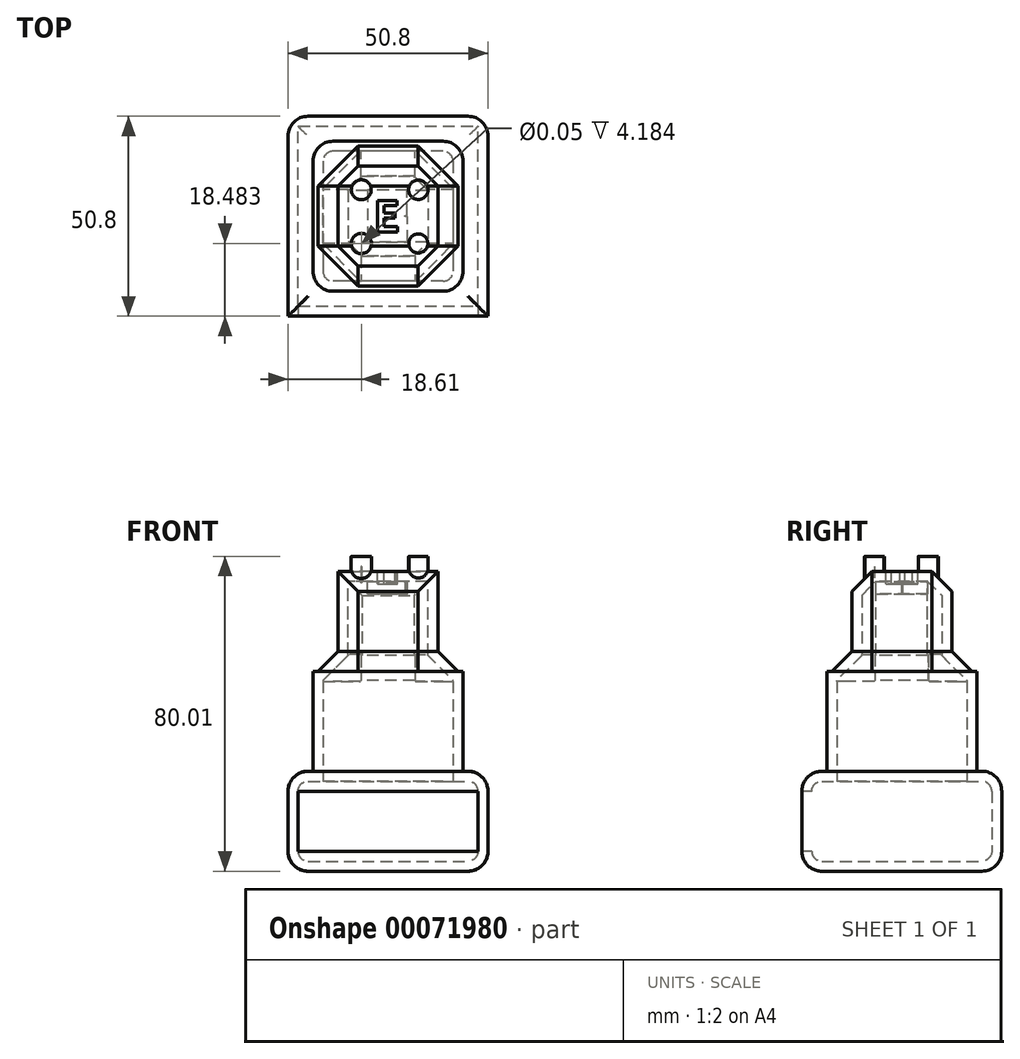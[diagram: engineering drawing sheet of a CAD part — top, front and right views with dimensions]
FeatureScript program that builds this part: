
annotation { "Feature Type Name" : "Feature", "Feature Type Description" : "" }
export const myFeature = defineFeature(function(context is Context, id is Id, definition is map)
    precondition{}
    {
        {
            var Q0;
            Q0=qCreatedBy(makeId("Top.planeOp"),FACE);
            var sketch = newSketch(context, id + "F0", { "sketchPlane" : qUnion([Q0])});
            skLineSegment(sketch, "E0.bottom", {"start": v(0, 0) * mm, "end": v(50.8, 0) * mm});
            skLineSegment(sketch, "E0.top", {"start": v(0, 50.8) * mm, "end": v(50.8, 50.8) * mm});
            skLineSegment(sketch, "E0.left", {"start": v(0, 0) * mm, "end": v(0, 50.8) * mm});
            skLineSegment(sketch, "E0.right", {"start": v(50.8, 0) * mm, "end": v(50.8, 50.8) * mm});
            skSolve(sketch);
        }
        {
            var Q0;
            Q0=makeQuery(id+"F0.imprint","IMPRINT",FACE,{"disambiguationData":[TD([[makeQuery(id+"F0.imprint","IMPRINT",EDGE,{"derivedFrom":sQuery(id+"F0.wireOp",EDGE,"E0.bottom")}),1.0]])]});
            extrude(context, id + "F1", {"entities" : qUnion([Q0]), "depth" : 25.4 * mm});
        }
        {
            var Q0;
            Q0=makeQuery(id+"F1.opExtrude","CAP_FACE",FACE,{"disambiguationData":[OSD([sQuery(id+"F0.wireOp",EDGE,"E0.bottom"),sQuery(id+"F0.wireOp",EDGE,"E0.top"),sQuery(id+"F0.wireOp",EDGE,"E0.left"),sQuery(id+"F0.wireOp",EDGE,"E0.right")])],"isStart":false});
            var sketch = newSketch(context, id + "F2", { "sketchPlane" : qUnion([Q0])});
            skLineSegment(sketch, "E1.rect.bottom", {"start": v(44.45, 44.45) * mm, "end": v(6.35, 44.45) * mm});
            skLineSegment(sketch, "E1.rect.top", {"start": v(44.45, 6.35) * mm, "end": v(6.35, 6.35) * mm});
            skLineSegment(sketch, "E1.rect.left", {"start": v(44.45, 44.45) * mm, "end": v(44.45, 6.35) * mm});
            skLineSegment(sketch, "E1.rect.right", {"start": v(6.35, 44.45) * mm, "end": v(6.35, 6.35) * mm});
            skPoint(sketch, "E1.rect.middle", {"position": v(25.4, 25.4) * mm});
            skPoint(sketch, "E1.rect.middle.positionSnap0", {"position": v(25.4, 50.8) * mm});
            skPoint(sketch, "E1.rect.middle.positionSnap1", {"position": v(0, 25.4) * mm});
            skPoint(sketch, "E1.rect.centerSnap0", {"position": v(25.4, 50.8) * mm});
            skPoint(sketch, "E1.rect.centerSnap1", {"position": v(0, 25.4) * mm});
            skSolve(sketch);
        }
        {
            var Q0;
            Q0=makeQuery(id+"F2.imprint","IMPRINT",FACE,{"disambiguationData":[TD([[makeQuery(id+"F2.imprint","IMPRINT",EDGE,{"derivedFrom":sQuery(id+"F2.wireOp",EDGE,"E1.rect.bottom")}),1.0]])]});
            extrude(context, id + "F3", {"entities" : qUnion([Q0]), "operationType" : NewBodyOperationType.ADD, "depth" : 25.4 * mm});
        }
        {
            var Q0;
            Q0=makeQuery(id+"F3.opExtrude","CAP_FACE",FACE,{"disambiguationData":[OSD([sQuery(id+"F2.wireOp",EDGE,"E1.rect.bottom"),sQuery(id+"F2.wireOp",EDGE,"E1.rect.top"),sQuery(id+"F2.wireOp",EDGE,"E1.rect.left"),sQuery(id+"F2.wireOp",EDGE,"E1.rect.right")])],"isStart":false});
            var sketch = newSketch(context, id + "F4", { "sketchPlane" : qUnion([Q0])});
            skLineSegment(sketch, "E2.rect.bottom", {"start": v(38.1, 38.1) * mm, "end": v(12.7, 38.1) * mm});
            skLineSegment(sketch, "E2.rect.top", {"start": v(38.1, 12.7) * mm, "end": v(12.7, 12.7) * mm});
            skLineSegment(sketch, "E2.rect.left", {"start": v(38.1, 38.1) * mm, "end": v(38.1, 12.7) * mm});
            skLineSegment(sketch, "E2.rect.right", {"start": v(12.7, 38.1) * mm, "end": v(12.7, 12.7) * mm});
            skPoint(sketch, "E2.rect.middle", {"position": v(25.4, 25.4) * mm});
            skPoint(sketch, "E2.rect.middle.positionSnap0", {"position": v(6.35, 25.4) * mm});
            skPoint(sketch, "E2.rect.middle.positionSnap1", {"position": v(25.4, 44.45) * mm});
            skPoint(sketch, "E2.rect.centerSnap0", {"position": v(6.35, 25.4) * mm});
            skPoint(sketch, "E2.rect.centerSnap1", {"position": v(25.4, 44.45) * mm});
            skSolve(sketch);
        }
        {
            var Q0;
            Q0=makeQuery(id+"F4.imprint","IMPRINT",FACE,{"disambiguationData":[TD([[makeQuery(id+"F4.imprint","IMPRINT",EDGE,{"derivedFrom":sQuery(id+"F4.wireOp",EDGE,"E2.rect.bottom")}),1.0]])]});
            extrude(context, id + "F5", {"entities" : qUnion([Q0]), "operationType" : NewBodyOperationType.ADD, "depth" : 25.4 * mm});
        }
        {
            var Q0;
            Q0=makeQuery(id+"F5.opExtrude","CAP_FACE",FACE,{"disambiguationData":[OSD([sQuery(id+"F4.wireOp",EDGE,"E2.rect.bottom"),sQuery(id+"F4.wireOp",EDGE,"E2.rect.top"),sQuery(id+"F4.wireOp",EDGE,"E2.rect.left"),sQuery(id+"F4.wireOp",EDGE,"E2.rect.right")])],"isStart":false});
            var sketch = newSketch(context, id + "F6", { "sketchPlane" : qUnion([Q0])});
            skCircle(sketch, "E3", {"center": v(18.6, 32.13) * mm, "radius": 2.54 * mm});
            skCircle(sketch, "E4", {"center": v(18.6, 18.48) * mm, "radius": 2.56 * mm});
            skCircle(sketch, "E5", {"center": v(33.1, 32.13) * mm, "radius": 2.47 * mm});
            skCircle(sketch, "E6", {"center": v(33.1, 18.48) * mm, "radius": 2.42 * mm});
            skSolve(sketch);
        }
        {
            var Q0;
            Q0=makeQuery(id+"F6.imprint","IMPRINT",FACE,{"disambiguationData":[TD([[makeQuery(id+"F6.imprint","IMPRINT",EDGE,{"derivedFrom":sQuery(id+"F6.wireOp",EDGE,"E3")}),1.0]])]});
            var Q1;
            Q1=makeQuery(id+"F6.imprint","IMPRINT",FACE,{"disambiguationData":[TD([[makeQuery(id+"F6.imprint","IMPRINT",EDGE,{"derivedFrom":sQuery(id+"F6.wireOp",EDGE,"E5")}),1.0]])]});
            var Q2;
            Q2=makeQuery(id+"F6.imprint","IMPRINT",FACE,{"disambiguationData":[TD([[makeQuery(id+"F6.imprint","IMPRINT",EDGE,{"derivedFrom":sQuery(id+"F6.wireOp",EDGE,"E6")}),1.0]])]});
            var Q3;
            Q3=makeQuery(id+"F6.imprint","IMPRINT",FACE,{"disambiguationData":[TD([[makeQuery(id+"F6.imprint","IMPRINT",EDGE,{"derivedFrom":sQuery(id+"F6.wireOp",EDGE,"E4")}),1.0]])]});
            extrude(context, id + "F7", {"entities" : qUnion([Q0, Q1, Q2, Q3]), "operationType" : NewBodyOperationType.ADD, "depth" : 3.8 * mm});
        }
        {
            var Q0;
            Q0=makeQuery(id+"F5.opExtrude","CAP_FACE",FACE,{"disambiguationData":[OSD([sQuery(id+"F4.wireOp",EDGE,"E2.rect.bottom"),sQuery(id+"F4.wireOp",EDGE,"E2.rect.top"),sQuery(id+"F4.wireOp",EDGE,"E2.rect.left"),sQuery(id+"F4.wireOp",EDGE,"E2.rect.right")])],"isStart":false});
            var sketch = newSketch(context, id + "F8", { "sketchPlane" : qUnion([Q0])});
            skText(sketch, "E7", { "text": "E", "fontName": "NotoSansCJKkr-Bold.otf"});
            const initialGuessF8  = {"E7": [0.0218, 0.0214, 1, 0, 0.00783]};
            skSetInitialGuess(sketch, initialGuessF8);
            skSolve(sketch);
        }
        {
            var Q0;
            Q0=makeQuery(id+"F8.imprint","IMPRINT",FACE,{"disambiguationData":[TD([[makeQuery(id+"F8.imprint","IMPRINT",EDGE,{"derivedFrom":sQuery(id+"F8.wireOp",EDGE,"E7.sketch_text.stroke-0")}),1.0]])]});
            extrude(context, id + "F9", {"entities" : qUnion([Q0]), "operationType" : NewBodyOperationType.REMOVE, "oppositeDirection" : true, "depth" : 3.17 * mm, "hasDraft" : true, "draftAngle" : .125 * degree});
        }
        {
            var Q0;
            Q0=makeQuery(id+"F5.opExtrude","SWEPT_FACE",FACE,{"disambiguationData":[OSD([sQuery(id+"F4.wireOp",EDGE,"E2.rect.top")])]});
            var Q1;
            Q1=makeQuery(id+"F5.opExtrude","SWEPT_FACE",FACE,{"disambiguationData":[OSD([sQuery(id+"F4.wireOp",EDGE,"E2.rect.bottom")])]});
            chamfer(context, id + "F10", {"entities" : qUnion([Q0, Q1]), "width" : 5.08 * mm, "tangentPropagation" : true});
        }
        {
            var Q0;
            Q0=makeQuery(id+"F3.opExtrude","CAP_EDGE",EDGE,{"disambiguationData":[OSD([sQuery(id+"F2.wireOp",EDGE,"E1.rect.right")])],"isStart":true});
            var Q1;
            Q1=makeQuery(id+"F3.opExtrude","CAP_EDGE",EDGE,{"disambiguationData":[OSD([sQuery(id+"F2.wireOp",EDGE,"E1.rect.bottom")])],"isStart":true});
            var Q2;
            Q2=makeQuery(id+"F3.opExtrude","CAP_EDGE",EDGE,{"disambiguationData":[OSD([sQuery(id+"F2.wireOp",EDGE,"E1.rect.left")])],"isStart":true});
            var Q3;
            Q3=makeQuery(id+"F3.opExtrude","CAP_EDGE",EDGE,{"disambiguationData":[OSD([sQuery(id+"F2.wireOp",EDGE,"E1.rect.top")])],"isStart":true});
            var Q4;
            Q4=makeQuery(id+"F3.opExtrude","SWEPT_EDGE",EDGE,{"disambiguationData":[OSD([sQuery(id+"F2.wireOp",EDGE,"E1.rect.top"),sQuery(id+"F2.wireOp",EDGE,"E1.rect.left")])]});
            var Q5;
            Q5=makeQuery(id+"F3.opExtrude","SWEPT_EDGE",EDGE,{"disambiguationData":[OSD([sQuery(id+"F2.wireOp",EDGE,"E1.rect.top"),sQuery(id+"F2.wireOp",EDGE,"E1.rect.right")])]});
            var Q6;
            Q6=makeQuery(id+"F3.opExtrude","SWEPT_EDGE",EDGE,{"disambiguationData":[OSD([sQuery(id+"F2.wireOp",EDGE,"E1.rect.bottom"),sQuery(id+"F2.wireOp",EDGE,"E1.rect.right")])]});
            var Q7;
            Q7=makeQuery(id+"F3.opExtrude","SWEPT_EDGE",EDGE,{"disambiguationData":[OSD([sQuery(id+"F2.wireOp",EDGE,"E1.rect.bottom"),sQuery(id+"F2.wireOp",EDGE,"E1.rect.left")])]});
            fillet(context, id + "F11", {"entities" : qUnion([Q0, Q1, Q2, Q3, Q4, Q5, Q6, Q7]), "radius" : 5.08 * mm, "tangentPropagation" : true, "allowEdgeOverflow" : false});
        }
        {
            var Q0;
            Q0=makeQuery(id+"F1.opExtrude","CAP_EDGE",EDGE,{"disambiguationData":[OSD([sQuery(id+"F0.wireOp",EDGE,"E0.bottom")])],"isStart":true});
            var Q1;
            Q1=makeQuery(id+"F1.opExtrude","CAP_EDGE",EDGE,{"disambiguationData":[OSD([sQuery(id+"F0.wireOp",EDGE,"E0.bottom")])],"isStart":false});
            var Q2;
            Q2=makeQuery(id+"F1.opExtrude","CAP_EDGE",EDGE,{"disambiguationData":[OSD([sQuery(id+"F0.wireOp",EDGE,"E0.left")])],"isStart":false});
            var Q3;
            Q3=makeQuery(id+"F1.opExtrude","CAP_EDGE",EDGE,{"disambiguationData":[OSD([sQuery(id+"F0.wireOp",EDGE,"E0.left")])],"isStart":true});
            var Q4;
            Q4=makeQuery(id+"F1.opExtrude","CAP_EDGE",EDGE,{"disambiguationData":[OSD([sQuery(id+"F0.wireOp",EDGE,"E0.top")])],"isStart":false});
            var Q5;
            Q5=makeQuery(id+"F1.opExtrude","CAP_EDGE",EDGE,{"disambiguationData":[OSD([sQuery(id+"F0.wireOp",EDGE,"E0.top")])],"isStart":true});
            var Q6;
            Q6=makeQuery(id+"F1.opExtrude","CAP_EDGE",EDGE,{"disambiguationData":[OSD([sQuery(id+"F0.wireOp",EDGE,"E0.right")])],"isStart":true});
            var Q7;
            Q7=makeQuery(id+"F1.opExtrude","CAP_EDGE",EDGE,{"disambiguationData":[OSD([sQuery(id+"F0.wireOp",EDGE,"E0.right")])],"isStart":false});
            fillet(context, id + "F12", {"entities" : qUnion([Q0, Q1, Q2, Q3, Q4, Q5, Q6, Q7]), "radius" : 5.08 * mm, "tangentPropagation" : true, "allowEdgeOverflow" : false});
        }
        {
            var Q0;
            Q0=makeQuery(id+"F1.opExtrude","SWEPT_FACE",FACE,{"disambiguationData":[OSD([sQuery(id+"F0.wireOp",EDGE,"E0.bottom")])]});
            shell(context, id + "F13", {"entities" : qUnion([Q0]), "thickness" : 2.54 * mm});
        }
        {
            var Q0;
            Q0=makeQuery(id+"F1.opExtrude","SWEPT_EDGE",EDGE,{"disambiguationData":[OSD([sQuery(id+"F0.wireOp",EDGE,"E0.top"),sQuery(id+"F0.wireOp",EDGE,"E0.left")])]});
            var Q1;
            Q1=makeQuery(id+"F1.opExtrude","SWEPT_EDGE",EDGE,{"disambiguationData":[OSD([sQuery(id+"F0.wireOp",EDGE,"E0.top"),sQuery(id+"F0.wireOp",EDGE,"E0.right")])]});
            fillet(context, id + "F14", {"entities" : qUnion([Q0, Q1]), "radius" : 5.08 * mm, "tangentPropagation" : true, "allowEdgeOverflow" : false});
        }
    });
